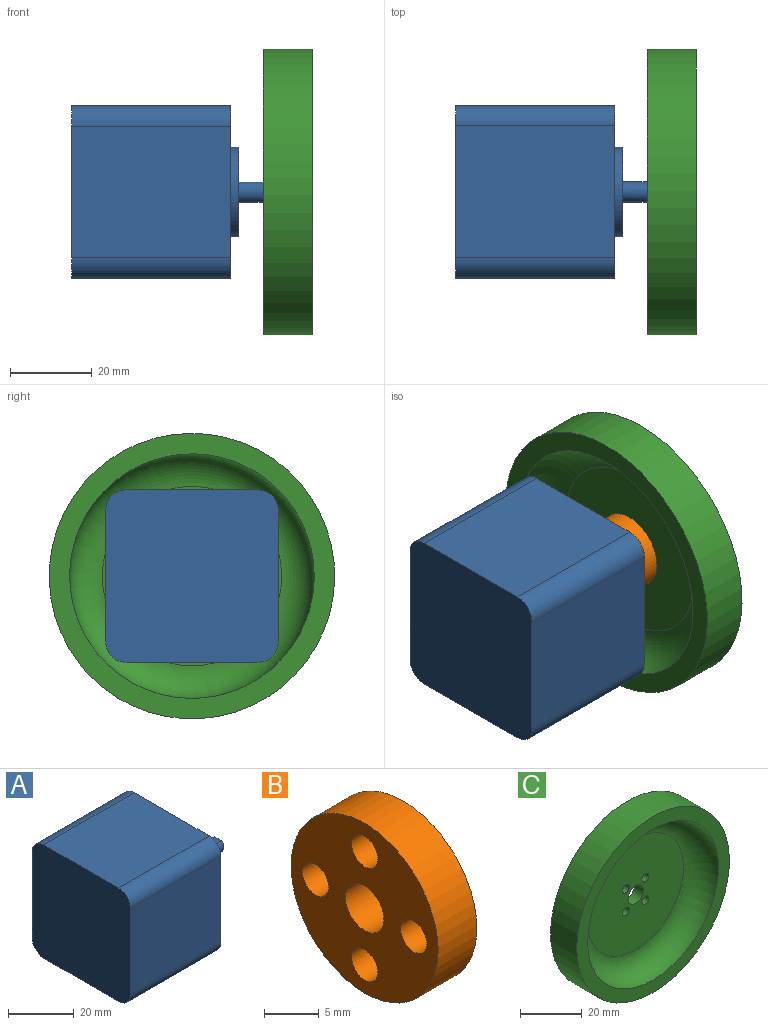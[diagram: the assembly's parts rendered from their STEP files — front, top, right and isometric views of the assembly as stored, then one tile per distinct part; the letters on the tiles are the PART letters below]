
ASSEMBLY  parts=3 mates=5
PART A: 24 faces, bbox 59x42.3x42.3 mm
  f0: plane 39x32.3mm, normal (0,0,-1), area 1259.7mm2, adj f4,f5,f20,f23
  f1: plane 39x32.3mm, normal (0,1,0), area 1259.7mm2, adj f4,f5,f20,f21
  f2: plane 39x32.3mm, normal (0,0,1), area 1259.7mm2, adj f4,f5,f21,f22
  f3: plane 39x32.3mm, normal (0,-1,0), area 1259.7mm2, adj f4,f5,f22,f23
  f4: plane 42.3x42.3mm, normal (1,0,0), area 1351.4mm2, adj f0,f1,f2,f3,f6,f13,f15,f17
  f5: plane 42.3x42.3mm, normal (-1,0,0), area 1767.8mm2, adj f0,f1,f2,f3,f20,f21,f22,f23
  f6: cylinder r=11mm len=22mm, axis (-1,0,0), area 138.2mm2, adj f4,f7
  f7: plane 22x22mm, normal (1,0,0), area 360.5mm2, adj f6,f8
  f8: cylinder r=2.5mm len=18mm, axis (-1,0,0), area 244.1mm2, adj f7,f9,f10,f11
  f9: plane 5x4.5mm, normal (1,0,0), area 18.6mm2, adj f8,f10
  f10: plane 12x3mm, normal (0,0,1), area 36mm2, adj f8,f9,f11
  f11: plane 3x0.5mm, normal (1,0,0), area 1mm2, adj f8,f10
  f12: cone r=0mm half-angle=59deg, axis (1,0,0), area 10.6mm2, adj f13
  f13: cylinder r=1.7mm len=4.5mm, axis (1,0,0), area 48.1mm2, adj f4,f12
  f14: cone r=0mm half-angle=59deg, axis (1,0,0), area 10.6mm2, adj f15
  f15: cylinder r=1.7mm len=4.5mm, axis (1,0,0), area 48.1mm2, adj f4,f14
  f16: cone r=0mm half-angle=59deg, axis (1,0,0), area 10.6mm2, adj f17
  f17: cylinder r=1.7mm len=4.5mm, axis (1,0,0), area 48.1mm2, adj f4,f16
  f18: cone r=0mm half-angle=59deg, axis (1,0,0), area 10.6mm2, adj f19
  f19: cylinder r=1.7mm len=4.5mm, axis (1,0,0), area 48.1mm2, adj f4,f18
  f20: cylinder r=5mm len=39mm, axis (1,0,0), area 306.3mm2, adj f0,f1,f4,f5
  f21: cylinder r=5mm len=39mm, axis (-1,0,0), area 306.3mm2, adj f1,f2,f4,f5
  f22: cylinder r=5mm len=39mm, axis (1,0,0), area 306.3mm2, adj f2,f3,f4,f5
  f23: cylinder r=5mm len=39mm, axis (-1,0,0), area 306.3mm2, adj f0,f3,f4,f5
PART B: 8 faces, bbox 5x19x19 mm
  f0: cylinder r=2.5mm len=5mm, axis (-1,0,0), area 78.5mm2, adj f2,f3
  f1: cylinder r=9.5mm len=19mm, axis (-1,0,0), area 298.5mm2, adj f2,f3
  f2: plane 19x19mm, normal (1,0,0), area 227.6mm2, adj f0,f1,f4,f5,f6,f7
  f3: plane 19x19mm, normal (-1,0,0), area 227.6mm2, adj f0,f1,f4,f5,f6,f7
  f4: cylinder r=1.7mm len=5mm, axis (-1,0,0), area 53.4mm2, adj f2,f3
  f5: cylinder r=1.7mm len=5mm, axis (-1,0,0), area 53.4mm2, adj f2,f3
  f6: cylinder r=1.7mm len=5mm, axis (-1,0,0), area 53.4mm2, adj f2,f3
  f7: cylinder r=1.7mm len=5mm, axis (-1,0,0), area 53.4mm2, adj f2,f3
PART C: 10 faces, bbox 70x12x70 mm
  f0: cylinder r=3.5mm len=7mm, axis (0,-1,0), area 88mm2, adj f1,f4
  f1: plane 70x70mm, normal (0,1,0), area 3777.8mm2, adj f0,f2,f6,f7,f8,f9
  f2: cylinder r=35mm len=70mm, axis (0,-1,0), area 2638.9mm2, adj f1,f3
  f3: plane 70x70mm, normal (0,-1,0), area 1021mm2, adj f2,f5
  f4: plane 44x44mm, normal (0,-1,0), area 1449.9mm2, adj f0,f5,f6,f7,f8,f9
  f5: torus R=22mm, axis (0,1,0), area 2139.2mm2, adj f3,f4
  f6: cylinder r=1.6mm len=4mm, axis (0,-1,0), area 40.2mm2, adj f1,f4
  f7: cylinder r=1.6mm len=4mm, axis (0,-1,0), area 40.2mm2, adj f1,f4
  f8: cylinder r=1.6mm len=4mm, axis (0,-1,0), area 40.2mm2, adj f1,f4
  f9: cylinder r=1.6mm len=4mm, axis (0,-1,0), area 40.2mm2, adj f1,f4
PLACE A t=(-18.55,0.83,-0.58)mm fixed
PLACE B rot(axis=(1,0,0),67.5deg) t=(31.45,0.83,-0.58)mm
PLACE C rot(axis=(-0.49,-0.49,-0.73),108deg) t=(34.45,0.83,-0.58)mm
MATE planar C.f0 <-> B.f4  axis (-1,0,0) through (36.45,0.83,-0.58)mm
MATE cylindrical C.f0 <-> A.f8  axis (-1,0,0) through (38.45,0.83,-0.58)mm
MATE planar A.f8 <-> C.f0  axis (1,0,0) through (40.45,0.83,-0.58)mm
MATE cylindrical B.f6 <-> C.f8  axis (-1,0,0) through (33.95,-1.6,-6.45)mm
MATE cylindrical B.f0 <-> A.f8  axis (-1,0,0) through (36.45,0.83,-0.58)mm
